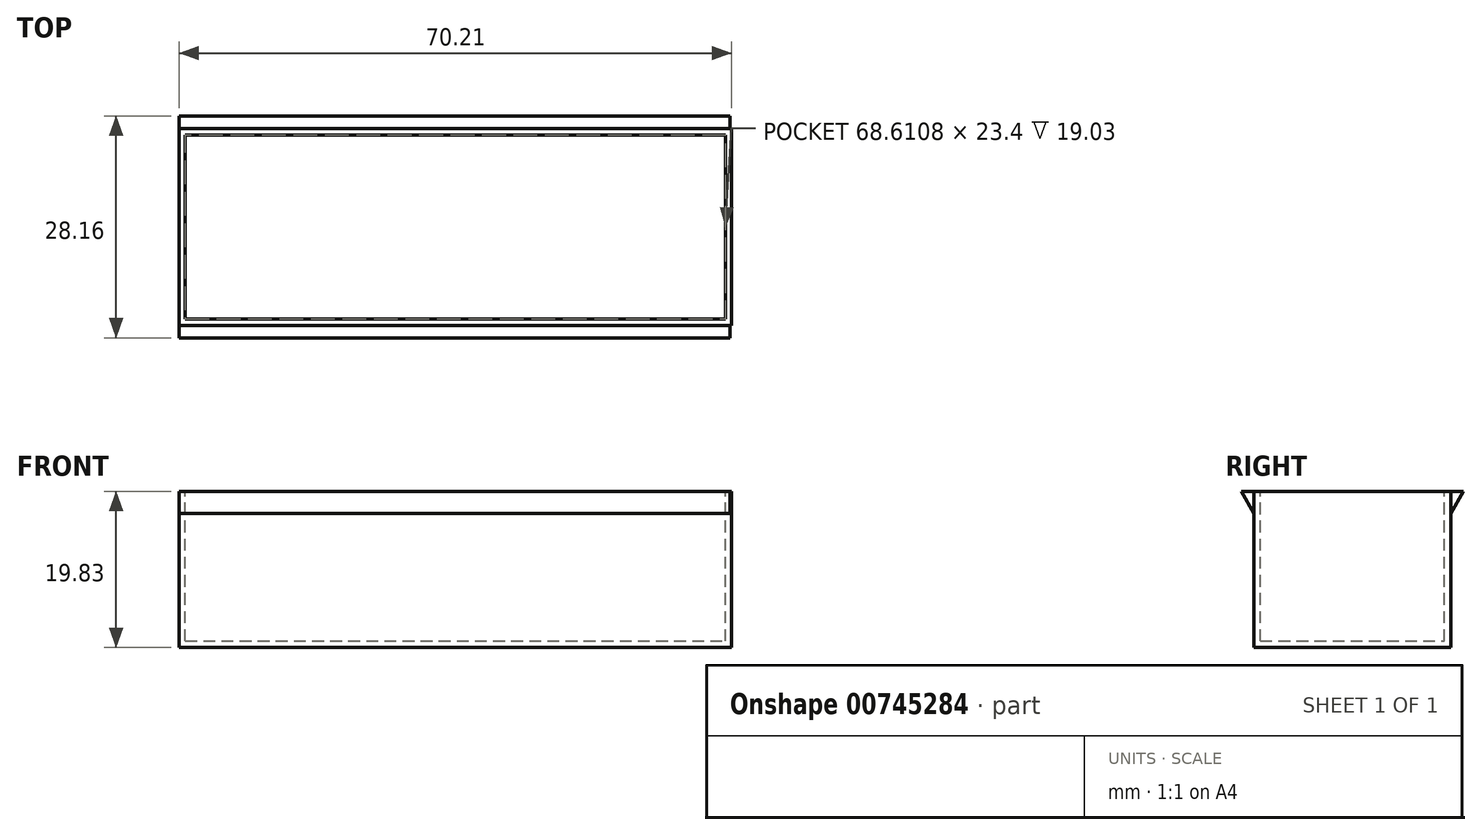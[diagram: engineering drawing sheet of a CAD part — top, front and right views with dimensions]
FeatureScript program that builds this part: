
annotation { "Feature Type Name" : "Feature", "Feature Type Description" : "" }
export const myFeature = defineFeature(function(context is Context, id is Id, definition is map)
    precondition{}
    {
        {
            var Q0;
            Q0=qCreatedBy(makeId("Front.planeOp"),FACE);
            var sketch = newSketch(context, id + "F0", { "sketchPlane" : qUnion([Q0])});
            skLineSegment(sketch, "E0.bottom", {"start": v(0, 0) * mm, "end": v(70.21, 0) * mm});
            skLineSegment(sketch, "E0.top", {"start": v(0, 19.83) * mm, "end": v(70.21, 19.83) * mm});
            skLineSegment(sketch, "E0.left", {"start": v(0, 0) * mm, "end": v(0, 19.83) * mm});
            skLineSegment(sketch, "E0.right", {"start": v(70.21, 0) * mm, "end": v(70.21, 19.83) * mm});
            skSolve(sketch);
        }
        {
            var Q0;
            Q0=makeQuery(id+"F0.imprint","IMPRINT",FACE,{"disambiguationData":[TD([[makeQuery(id+"F0.imprint","IMPRINT",EDGE,{"derivedFrom":sQuery(id+"F0.wireOp",EDGE,"E0.bottom")}),1.0]])]});
            extrude(context, id + "F1", {"entities" : qUnion([Q0]), "depth" : 25 * mm, "offsetDistance" : 25 * mm});
        }
        {
            var Q0;
            Q0=makeQuery(id+"F1.opExtrude","SWEPT_FACE",FACE,{"disambiguationData":[OSD([sQuery(id+"F0.wireOp",EDGE,"E0.top")])]});
            shell(context, id + "F2", {"entities" : qUnion([Q0]), "thickness" : 0.8 * mm});
        }
        {
            var Q0;
            Q0=makeQuery(id+"F1.opExtrude","SWEPT_FACE",FACE,{"disambiguationData":[OSD([sQuery(id+"F0.wireOp",EDGE,"E0.left")])]});
            var sketch = newSketch(context, id + "F3", { "sketchPlane" : qUnion([Q0])});
            skLineSegment(sketch, "E1", {"start": v(25, 19.83) * mm, "end": v(26.58, 19.83) * mm});
            skLineSegment(sketch, "E2", {"start": v(26.58, 19.83) * mm, "end": v(25, 17.05) * mm});
            skLineSegment(sketch, "E3", {"start": v(25, 17.05) * mm, "end": v(25, 19.83) * mm});
            skLineSegment(sketch, "E4", {"start": v(12.5, 19.83) * mm, "end": v(12.5, 0) * mm, "construction": true});
            skLineSegment(sketch, "E5.MirrorCS", {"start": v(-1.58, 19.83) * mm, "end": v(0, 17.05) * mm});
            skLineSegment(sketch, "E6.MirrorCS", {"start": v(0, 19.83) * mm, "end": v(-1.58, 19.83) * mm});
            skLineSegment(sketch, "E7.MirrorCS", {"start": v(0, 17.05) * mm, "end": v(0, 19.83) * mm});
            skSolve(sketch);
        }
        {
            var Q0;
            Q0=makeQuery(id+"F3.imprint","IMPRINT",FACE,{"disambiguationData":[TD([[makeQuery(id+"F3.imprint","IMPRINT",EDGE,{"derivedFrom":sQuery(id+"F3.wireOp",EDGE,"E1")}),-1.0]])]});
            var Q1;
            Q1=makeQuery(id+"F3.imprint","IMPRINT",FACE,{"disambiguationData":[TD([[makeQuery(id+"F3.imprint","IMPRINT",EDGE,{"derivedFrom":sQuery(id+"F3.wireOp",EDGE,"E5.MirrorCS")}),1.0]])]});
            extrude(context, id + "F4", {"entities" : qUnion([Q0, Q1]), "oppositeDirection" : true, "depth" : 70 * mm, "offsetDistance" : 25 * mm});
        }
    });
